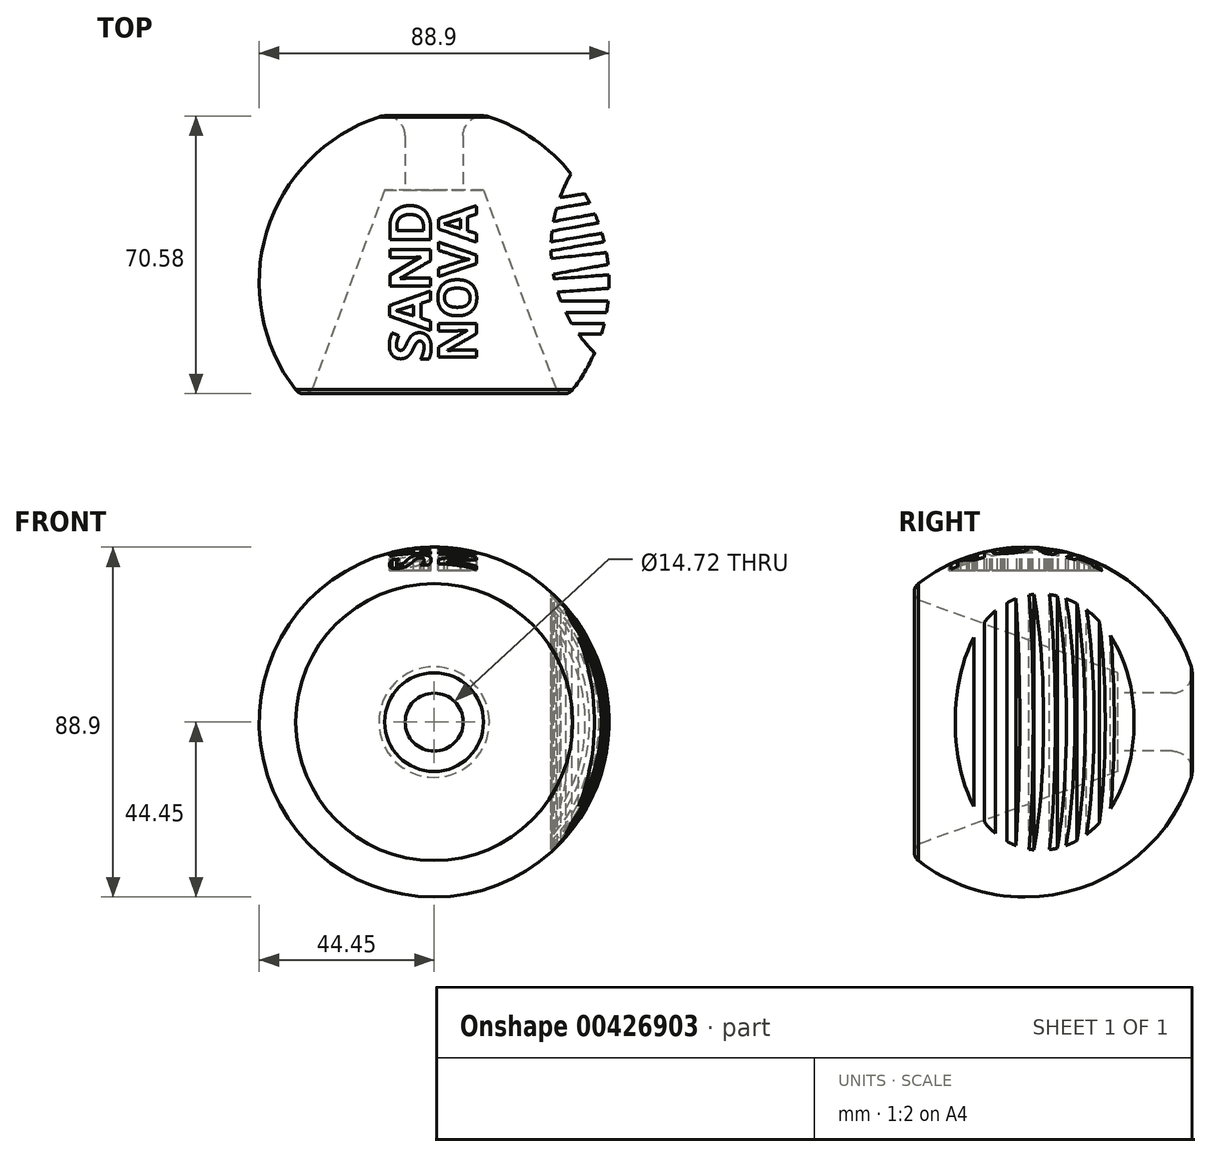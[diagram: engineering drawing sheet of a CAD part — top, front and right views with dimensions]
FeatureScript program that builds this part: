
annotation { "Feature Type Name" : "Feature", "Feature Type Description" : "" }
export const myFeature = defineFeature(function(context is Context, id is Id, definition is map)
    precondition{}
    {
        {
            var Q0;
            Q0=qCreatedBy(makeId("Front.planeOp"),FACE);
            var sketch = newSketch(context, id + "F0", { "sketchPlane" : qUnion([Q0])});
            skArc(sketch, "E0", {"start": v(0, 44.45) * mm, "mid": v(-44.45, 0) * mm, "end": v(0, -44.45) * mm});
            skLineSegment(sketch, "E1", {"start": v(0, 44.45) * mm, "end": v(0, -44.45) * mm});
            skSolve(sketch);
        }
        {
            var Q0;
            Q0 = qSketchRegion(id + "F0", true);
            var Q1;
            Q1=sQuery(id+"F0.wireOp",EDGE,"E1");
            revolve(context, id + "F1", {"entities" : qUnion([Q0]), "axis" : qUnion([Q1]), "revolveType" : RevolveType.FULL});
        }
        {
            var Q0;
            Q0=qCreatedBy(makeId("Front.planeOp"),FACE);
            cPlane(context, id + "F2", {"entities" : qUnion([Q0]), "cplaneType" : CPlaneType.OFFSET, "offset" : 48.26 * mm, "width" : 152.4 * mm, "height" : 152.4 * mm});
        }
        {
            var Q0;
            Q0=qCreatedBy(id+"F2.planeOp",FACE);
            var sketch = newSketch(context, id + "F3", { "sketchPlane" : qUnion([Q0])});
            skCircle(sketch, "E2", {"center": v(0, 0) * mm, "radius": 38.71 * mm});
            skSolve(sketch);
        }
        {
            var Q0;
            Q0 = qSketchRegion(id + "F3", true);
            extrude(context, id + "F4", {"entities" : qUnion([Q0]), "operationType" : NewBodyOperationType.REMOVE, "oppositeDirection" : true, "depth" : 71.88 * mm, "hasDraft" : true, "draftAngle" : 20 * degree, "draftPullDirection" : true});
        }
        {
            var Q0;
            Q0=qCreatedBy(makeId("Top.planeOp"),FACE);
            var sketch = newSketch(context, id + "F5", { "sketchPlane" : qUnion([Q0])});
            skArc(sketch, "E3", {"start": v(29.96, 13.15) * mm, "mid": v(29.82, 11.77) * mm, "end": v(29.74, 10.4) * mm});
            skLineSegment(sketch, "E4", {"start": v(30.33, 15.6) * mm, "end": v(42.5, 17.79) * mm});
            skLineSegment(sketch, "E5", {"start": v(42.5, 17.79) * mm, "end": v(42.91, 15.48) * mm});
            skLineSegment(sketch, "E6", {"start": v(42.91, 15.48) * mm, "end": v(29.96, 13.15) * mm});
            skLineSegment(sketch, "E7", {"start": v(29.74, 10.4) * mm, "end": v(43.91, 12.84) * mm});
            skLineSegment(sketch, "E8", {"start": v(43.91, 12.84) * mm, "end": v(44.29, 10.66) * mm});
            skLineSegment(sketch, "E9", {"start": v(44.29, 10.66) * mm, "end": v(29.71, 8.14) * mm});
            skLineSegment(sketch, "E10", {"start": v(29.8, 6.16) * mm, "end": v(45.6, 7.89) * mm});
            skLineSegment(sketch, "E11", {"start": v(45.6, 7.89) * mm, "end": v(46.1, 5.04) * mm});
            skLineSegment(sketch, "E12", {"start": v(46.1, 5.04) * mm, "end": v(30.3, 2.2) * mm});
            skLineSegment(sketch, "E13", {"start": v(30.53, 1) * mm, "end": v(46.36, 2.2) * mm});
            skLineSegment(sketch, "E14", {"start": v(46.36, 2.2) * mm, "end": v(46.61, -1.21) * mm});
            skLineSegment(sketch, "E15", {"start": v(46.61, -1.21) * mm, "end": v(31.4, -2.35) * mm});
            skLineSegment(sketch, "E16", {"start": v(32.21, -4.67) * mm, "end": v(47.2, -4.67) * mm});
            skLineSegment(sketch, "E17", {"start": v(47.2, -4.67) * mm, "end": v(46.44, -7.53) * mm});
            skLineSegment(sketch, "E18", {"start": v(46.44, -7.53) * mm, "end": v(33.45, -7.53) * mm});
            skArc(sketch, "E19.trimOffspring", {"start": v(29.71, 8.14) * mm, "mid": v(29.75, 7.15) * mm, "end": v(29.8, 6.16) * mm});
            skArc(sketch, "E20.trimOffspring", {"start": v(31.4, -2.35) * mm, "mid": v(31.79, -3.51) * mm, "end": v(32.21, -4.67) * mm});
            skArc(sketch, "E21.trimOffspring", {"start": v(33.45, -7.53) * mm, "mid": v(34.18, -8.96) * mm, "end": v(34.97, -10.36) * mm});
            skLineSegment(sketch, "E22", {"start": v(30.3, 2.2) * mm, "end": v(30.53, 1) * mm});
            skLineSegment(sketch, "E23", {"start": v(31.08, 18.9) * mm, "end": v(41.24, 20.63) * mm});
            skLineSegment(sketch, "E24", {"start": v(41.24, 20.63) * mm, "end": v(39.85, 22.87) * mm});
            skLineSegment(sketch, "E25", {"start": v(39.85, 22.87) * mm, "end": v(31.98, 21.69) * mm});
            skLineSegment(sketch, "E26", {"start": v(34.97, -10.36) * mm, "end": v(44.93, -10.36) * mm});
            skLineSegment(sketch, "E27", {"start": v(44.93, -10.36) * mm, "end": v(44.93, -13) * mm});
            skLineSegment(sketch, "E28", {"start": v(44.93, -13) * mm, "end": v(36.69, -13) * mm});
            skArc(sketch, "E29.trimOffspring", {"start": v(31.08, 18.9) * mm, "mid": v(30.67, 17.26) * mm, "end": v(30.33, 15.6) * mm});
            skArc(sketch, "E30.trimOffspring", {"start": v(36.69, -13) * mm, "mid": v(104.57, 13.88) * mm, "end": v(31.98, 21.69) * mm});
            skSolve(sketch);
        }
        {
            var Q0;
            Q0 = qSketchRegion(id + "F5", true);
            extrude(context, id + "F6", {"entities" : qUnion([Q0]), "operationType" : NewBodyOperationType.REMOVE, "endBound" : BoundingType.SYMMETRIC, "oppositeDirection" : true, "depth" : 114.8 * mm});
        }
        {
            var Q0;
            Q0=makeQuery(id+"F4.boolean.opBoolean","INTERSECT",EDGE,{"derivedFrom":[makeQuery(id+"F1.opRevolve","SWEPT_FACE",FACE,{"disambiguationData":[OSD([sQuery(id+"F0.wireOp",EDGE,"E0")])]}),makeQuery(id+"F4.opExtrude","SWEPT_FACE",FACE,{"disambiguationData":[OSD([sQuery(id+"F3.wireOp",EDGE,"E2")])]})]});
            fillet(context, id + "F7", {"entities" : qUnion([Q0]), "radius" : 2.54 * mm, "tangentPropagation" : true, "allowEdgeOverflow" : false});
        }
        {
            var Q0;
            Q0=qCreatedBy(id+"F2.planeOp",FACE);
            var sketch = newSketch(context, id + "F8", { "sketchPlane" : qUnion([Q0])});
            skCircle(sketch, "E31", {"center": v(0, 0) * mm, "radius": 7.36 * mm});
            skSolve(sketch);
        }
        {
            var Q0;
            Q0 = qSketchRegion(id + "F8", true);
            extrude(context, id + "F9", {"entities" : qUnion([Q0]), "operationType" : NewBodyOperationType.REMOVE, "oppositeDirection" : true, "depth" : 122.17 * mm});
        }
        {
            var Q0;
            Q0=makeQuery(id+"F9.boolean.opBoolean","INTERSECT",EDGE,{"derivedFrom":[makeQuery(id+"F1.opRevolve","SWEPT_FACE",FACE,{"disambiguationData":[OSD([sQuery(id+"F0.wireOp",EDGE,"E0")])]}),makeQuery(id+"F9.opExtrude","SWEPT_FACE",FACE,{"disambiguationData":[OSD([sQuery(id+"F8.wireOp",EDGE,"E31")])]})]});
            fillet(context, id + "F10", {"entities" : qUnion([Q0]), "radius" : 5.08 * mm, "tangentPropagation" : true, "allowEdgeOverflow" : false});
        }
        {
            var Q0;
            Q0=qCreatedBy(makeId("Top.planeOp"),FACE);
            cPlane(context, id + "F11", {"entities" : qUnion([Q0]), "cplaneType" : CPlaneType.OFFSET, "offset" : 50.8 * mm, "width" : 152.4 * mm, "height" : 152.4 * mm});
        }
        {
            var Q0;
            Q0=qCreatedBy(id+"F11.planeOp",FACE);
            var sketch = newSketch(context, id + "F12", { "sketchPlane" : qUnion([Q0])});
            skText(sketch, "E32", { "text": "SAND", "fontName": "OpenSans-Bold.ttf"});
            skText(sketch, "E33", { "text": "NOVA", "fontName": "OpenSans-Bold.ttf"});
            const initialGuessF12  = {"E32": [-0.00088, -0.02008, 0, 1, 0.01045], "E33": [0.01072, -0.02009, 0, 1, 0.0097]};
            skSetInitialGuess(sketch, initialGuessF12);
            skSolve(sketch);
        }
        {
            var Q0;
            Q0 = qSketchRegion(id + "F12", true);
            extrude(context, id + "F13", {"entities" : qUnion([Q0]), "operationType" : NewBodyOperationType.REMOVE, "oppositeDirection" : true, "depth" : 12.27 * mm});
        }
    });
